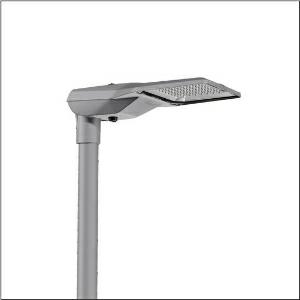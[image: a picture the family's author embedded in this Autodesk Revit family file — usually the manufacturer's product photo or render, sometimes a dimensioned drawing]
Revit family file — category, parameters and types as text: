
# Revit family: streetlight_sl_21_iq_midi___p0_8a_5xe3u31y08nb_1433
name_source: partatom
category: Lighting Fixtures
units: mm (PartAtom-declared; Revit-internal decimal feet)

## family parameters
Cut with Voids When Loaded = No
Host = Face
Light Source = No
Part Type = Normal
Room Calculation Point = No
Round Connector Dimension = Use Diameter
Shared = No

## types (1)
- --- (1 x LED, 21740 lm, 136.6 W, 3000K)
    Apparent Load = 137 VA
    CIE Flux Codes = 36 69 97 100 100
    Color Rendering = 70
    Color Temperature = 3000K
    Default Elevation = 1800 mm
    Description = Streetlight SL 21 iQ midi, mast luminaire, primary light control with lens, of PMMA, primary optical cover: cover, of toughened safety glass, transparent, light distribution: P0.8a, light emission: direct distribution, primary light characteristic: asymmetric, installation type: post-top, side-entry, LED, High Power LED, rated luminous flux: 21.740lm, luminous efficacy: 159lm/W, light colour: 730, colour temperature: 3000K, control gear: iQ-Street Remote, D4i with power reduction, control: pre-setting: logarithmic dimming characteristic, Street-Remote, Auto-Match, Temp-Guard, Lumen-Switch, Night-Set, Smart-Wire, Light-Fading, Desk-Remote (wireless, voltage-free reading and setting of iQ features in the workshop via application-optimized NFC function/RFID function), optimised constant luminous flux control (CLO 2.0), mains connection: 230..240V, AC, 50/60Hz, start of lifetime: 137W, end of service life: 144W, reduction: 61W, luminaire housing, of diecast aluminium, powder-coated, Siteco® metallic grey (DB 702S), corrosivity category C5 mid according to DIN EN ISO 12944, please order mast flange separately, inclination adjustable: 0°, 5°, 10°, 15°, sealing non-destructively replaceable, multi-level sealing system, length: 644mm, width: 335mm, height: 110mm, mast flange for spigot size: 42mm (side-entry): 5XC10008XM4, 60/48mm (side-entry/post-top): 5XC10108XM2, 76/60mm (side-entry/post-top): 5XC10108XM1, mounting height: 4..8m, Smart Interface below and above, protection rating (complete): IP66, insulation class (complete): insulation class II (safety insulation), certification: CE, ENEC, ENEC+, VDE, impact resistance: IK10, permissible operating ambient temperature for outdoor applications: -40..+50°C, standard-compliant lighting for roads and squares, packaging unit: 1 piece

Light Distribution: P0.8a
    Height = 111 mm
    Lamp = 1 x LED
    Lamp Light Flux = 21740 lm
    Lamp Power = 136.6 W
    Lamp count = 1
    Length = 644 mm
    Luminous efficacy = 159 lm/W
    Manufacturer = Siteco
    ModVariant = No
    Model = 5XE3U31Y08NB
    Number of Poles = 1
    OnlyDefault = Yes
    Power Factor = 1
    Product Name = Streetlight SL 21 iQ midi | P0.8a
    Product group = mast luminaire | pylon top
    ProductGroupID = 6100
    Protection Class = Protection class II
    Protection Degree = IP 66
    RLX_Detail_Level = 1
    RLX_Emergency_Light_Flux = 0 lm
    RLX_Emergency_Type = 0
    RLX_Emergency_Type_DB = No
    RlxData = <blob elided: 91353 chars, md5=c4f638dd>
    Socket = socket
    Standby Power = 0 W
    System Light Flux = 21740 lm
    System Power = 137 W
    Type Comments = factory setting: luminous flux: 100 % | dim-lin: 254 | 733 mA
    Type Image = l_1004304.jpg
    URL = http://relux.com
    VarID = @adj_093507
    Voltage = 0 V
    Weight = 0.00 kg
    Width = 336 mm

## geometry (parser evidence)
native form markers: Blend x4, Sweep x9
no freeform markers — native parametric forms only
